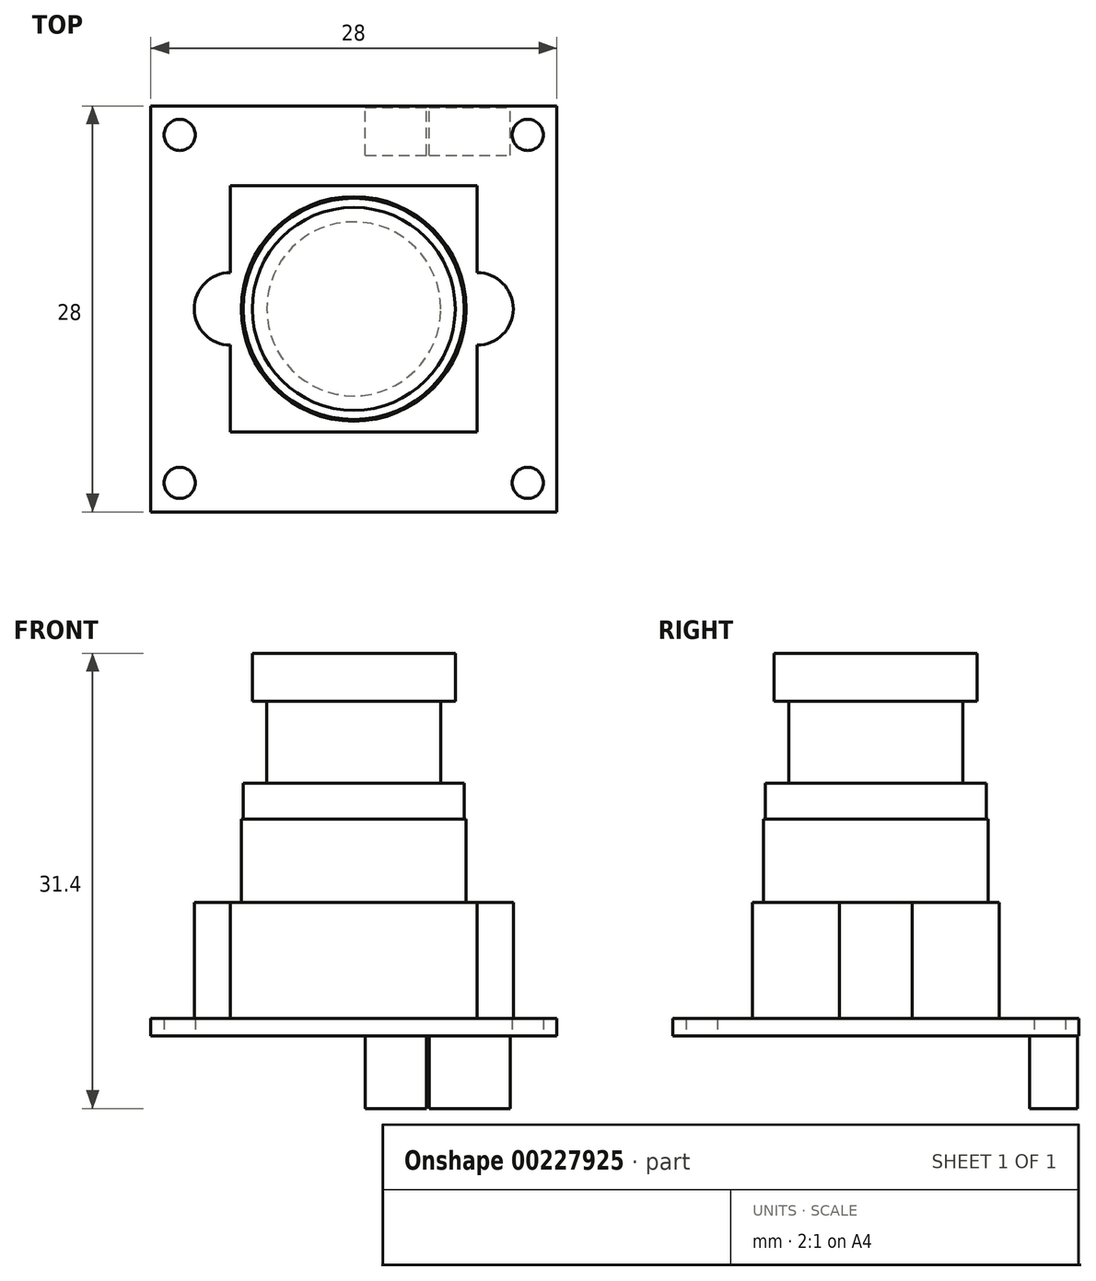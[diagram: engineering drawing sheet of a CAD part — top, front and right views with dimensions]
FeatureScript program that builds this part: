
annotation { "Feature Type Name" : "Feature", "Feature Type Description" : "" }
export const myFeature = defineFeature(function(context is Context, id is Id, definition is map)
    precondition{}
    {
        {
            var Q0;
            Q0=qCreatedBy(makeId("Top.planeOp"),FACE);
            var sketch = newSketch(context, id + "F0", { "sketchPlane" : qUnion([Q0])});
            skLineSegment(sketch, "E0.bottom", {"start": v(-14, 14) * mm, "end": v(14, 14) * mm});
            skLineSegment(sketch, "E0.top", {"start": v(-14, -14) * mm, "end": v(14, -14) * mm});
            skLineSegment(sketch, "E0.left", {"start": v(-14, 14) * mm, "end": v(-14, -14) * mm});
            skLineSegment(sketch, "E0.right", {"start": v(14, 14) * mm, "end": v(14, -14) * mm});
            skLineSegment(sketch, "E1", {"start": v(-14, 14) * mm, "end": v(14, -14) * mm, "construction": true});
            skCircle(sketch, "E2", {"center": v(-12, 12) * mm, "radius": 1.07 * mm});
            skCircle(sketch, "E3.1.0", {"center": v(-12, -12) * mm, "radius": 1.07 * mm});
            skCircle(sketch, "E3.2.0", {"center": v(12, -12) * mm, "radius": 1.07 * mm});
            skCircle(sketch, "E3.3.0", {"center": v(12, 12) * mm, "radius": 1.07 * mm});
            skPoint(sketch, "E3.center", {"position": v(0, 0) * mm});
            skSolve(sketch);
        }
        {
            var Q0;
            Q0 = qSketchRegion(id + "F0", true);
            extrude(context, id + "F1", {"entities" : qUnion([Q0]), "depth" : 1.2 * mm});
        }
        {
            var Q0;
            Q0=makeQuery(id+"F1.opExtrude","CAP_FACE",FACE,{"disambiguationData":[OSD([sQuery(id+"F0.wireOp",EDGE,"E0.bottom"),sQuery(id+"F0.wireOp",EDGE,"E0.top"),sQuery(id+"F0.wireOp",EDGE,"E0.left"),sQuery(id+"F0.wireOp",EDGE,"E0.right"),sQuery(id+"F0.wireOp",EDGE,"E2"),sQuery(id+"F0.wireOp",EDGE,"E3.1.0"),sQuery(id+"F0.wireOp",EDGE,"E3.2.0"),sQuery(id+"F0.wireOp",EDGE,"E3.3.0")])],"isStart":false});
            var sketch = newSketch(context, id + "F2", { "sketchPlane" : qUnion([Q0])});
            skLineSegment(sketch, "E4.bottom", {"start": v(-8.5, 8.5) * mm, "end": v(8.5, 8.5) * mm});
            skLineSegment(sketch, "E4.top", {"start": v(-8.5, -8.5) * mm, "end": v(8.5, -8.5) * mm});
            skLineSegment(sketch, "E4.left", {"start": v(-8.5, 8.5) * mm, "end": v(-8.5, 2.5) * mm});
            skLineSegment(sketch, "E4.right", {"start": v(8.5, 8.5) * mm, "end": v(8.5, 2.5) * mm});
            skArc(sketch, "E5", {"start": v(-8.5, 2.5) * mm, "mid": v(-11, 0) * mm, "end": v(-8.5, -2.5) * mm});
            skArc(sketch, "E6", {"start": v(8.5, -2.5) * mm, "mid": v(11, 0) * mm, "end": v(8.5, 2.5) * mm});
            skLineSegment(sketch, "E7.trimOffspring", {"start": v(-8.5, -2.5) * mm, "end": v(-8.5, -8.5) * mm});
            skLineSegment(sketch, "E8.trimOffspring", {"start": v(8.5, -2.5) * mm, "end": v(8.5, -8.5) * mm});
            skSolve(sketch);
        }
        {
            var Q0;
            Q0=makeQuery(id+"F2.imprint","IMPRINT",FACE,{"disambiguationData":[TD([[makeQuery(id+"F2.imprint","IMPRINT",EDGE,{"derivedFrom":sQuery(id+"F2.wireOp",EDGE,"E4.bottom")}),-1.0]])]});
            extrude(context, id + "F3", {"entities" : qUnion([Q0]), "depth" : 8 * mm});
        }
        {
            var Q0;
            Q0=qCreatedBy(makeId("Front.planeOp"),FACE);
            var sketch = newSketch(context, id + "F4", { "sketchPlane" : qUnion([Q0])});
            skLineSegment(sketch, "E9", {"start": v(0, 26.4) * mm, "end": v(-7, 26.4) * mm});
            skLineSegment(sketch, "E10", {"start": v(-7, 26.4) * mm, "end": v(-7, 23.1) * mm});
            skLineSegment(sketch, "E11", {"start": v(-7, 23.1) * mm, "end": v(-6, 23.1) * mm});
            skLineSegment(sketch, "E12", {"start": v(-6, 23.1) * mm, "end": v(-6, 17.45) * mm});
            skLineSegment(sketch, "E13", {"start": v(-6, 17.45) * mm, "end": v(-7.62, 17.45) * mm});
            skLineSegment(sketch, "E14", {"start": v(-7.62, 17.45) * mm, "end": v(-7.62, 14.95) * mm});
            skLineSegment(sketch, "E15", {"start": v(-7.62, 14.95) * mm, "end": v(-7.75, 14.95) * mm});
            skLineSegment(sketch, "E16", {"start": v(-7.75, 14.95) * mm, "end": v(-7.75, 9.2) * mm});
            skLineSegment(sketch, "E17", {"start": v(0, 9.2) * mm, "end": v(0, 26.4) * mm});
            skLineSegment(sketch, "E18.0", {"start": v(-7.75, 9.2) * mm, "end": v(0, 9.2) * mm});
            skSolve(sketch);
        }
        {
            var Q0;
            Q0=makeQuery(id+"F4.imprint","IMPRINT",FACE,{"disambiguationData":[TD([[makeQuery(id+"F4.imprint","IMPRINT",EDGE,{"derivedFrom":sQuery(id+"F4.wireOp",EDGE,"E9")}),1.0]])]});
            var Q1;
            Q1=sQuery(id+"F4.wireOp",EDGE,"E17");
            revolve(context, id + "F5", {"operationType" : NewBodyOperationType.ADD, "entities" : qUnion([Q0]), "axis" : qUnion([Q1]), "revolveType" : RevolveType.FULL});
        }
        {
            var Q0;
            Q0=makeQuery(id+"F1.opExtrude","CAP_FACE",FACE,{"disambiguationData":[OSD([sQuery(id+"F0.wireOp",EDGE,"E0.bottom"),sQuery(id+"F0.wireOp",EDGE,"E0.top"),sQuery(id+"F0.wireOp",EDGE,"E0.left"),sQuery(id+"F0.wireOp",EDGE,"E0.right"),sQuery(id+"F0.wireOp",EDGE,"E2"),sQuery(id+"F0.wireOp",EDGE,"E3.1.0"),sQuery(id+"F0.wireOp",EDGE,"E3.2.0"),sQuery(id+"F0.wireOp",EDGE,"E3.3.0")])],"isStart":true});
            var sketch = newSketch(context, id + "F6", { "sketchPlane" : qUnion([Q0])});
            skLineSegment(sketch, "E19.bottom", {"start": v(0.8, -10.6) * mm, "end": v(5, -10.6) * mm});
            skLineSegment(sketch, "E19.top", {"start": v(0.8, -13.9) * mm, "end": v(5, -13.9) * mm});
            skLineSegment(sketch, "E19.left", {"start": v(0.8, -10.6) * mm, "end": v(0.8, -13.9) * mm});
            skLineSegment(sketch, "E19.right", {"start": v(5, -10.6) * mm, "end": v(5, -13.9) * mm});
            skLineSegment(sketch, "E20.bottom", {"start": v(5.2, -10.6) * mm, "end": v(10.8, -10.6) * mm});
            skLineSegment(sketch, "E20.top", {"start": v(5.2, -13.9) * mm, "end": v(10.8, -13.9) * mm});
            skLineSegment(sketch, "E20.left", {"start": v(5.2, -10.6) * mm, "end": v(5.2, -13.9) * mm});
            skLineSegment(sketch, "E20.right", {"start": v(10.8, -10.6) * mm, "end": v(10.8, -13.9) * mm});
            skSolve(sketch);
        }
        {
            var Q0;
            Q0 = qSketchRegion(id + "F6", true);
            extrude(context, id + "F7", {"entities" : qUnion([Q0]), "operationType" : NewBodyOperationType.ADD, "depth" : 5 * mm});
        }
    });
